# Revit family: Gaius Life Basin_
name_source: partatom
category: Plumbing Fixtures
revit_build: Autodesk Revit Architecture 2012 (Build: 20110916_2132(x64)
units: mm (PartAtom-declared; Revit-internal decimal feet)

## types (20) — shared parameters
Drain Pipe Material = Chrome - Polished
Manufacturer = Korpinen Oy
URL = www.korpinen.com
Vent Connection = No

## per-type parameters (varying)
| type | Basin Type | Cabinet Type | Height | Model |
| 6700 | Gaius Life : 6700 | None | 850 mm  [stored 2.78871 ft] | 6700 Gaius Life |
| 6701 | Gaius Life : 6701 | None | 850 mm  [stored 2.78871 ft] | 6701 Gaius Life |
| 6706 | Gaius Life : 6706 | None | 850 mm  [stored 2.78871 ft] | 6706 Gaius Life |
| 6707 | Gaius Life : 6707 | None | 850 mm  [stored 2.78871 ft] | 6707 Gaius Life |
| 6709 | Gaius Life : 6709 | None | 850 mm  [stored 2.78871 ft] | 6709 Gaius Life |
| 6708 | Gaius Life : 6708 | None | 850 mm  [stored 2.78871 ft] | 6708 Gaius Life |
| 6702 | Gaius Life : 6702 | None | 850 mm  [stored 2.78871 ft] | 6702 Gaius Life |
| 6703 | Gaius Life : 6703 | None | 850 mm  [stored 2.78871 ft] | 6703 Gaius Life |
| 6704 | Gaius Life : 6704 | None | 850 mm  [stored 2.78871 ft] | 6704 Gaius Life |
| 6705 | Gaius Life : 6705 | None | 850 mm  [stored 2.78871 ft] | 6705 Gaius Life |
| 6700 with Drawer Cabinet | Gaius Life : 6700 | Life - Under Basin Cabinet : 2000-1001 | 850 mm  [stored 2.78871 ft] | 6700 Gaius Life + 2000-1001 |
| 6701 with Drawer Cabinet | Gaius Life : 6701 | Life - Under Basin Cabinet : 2000-1001 | 850 mm  [stored 2.78871 ft] | 6701 Gaius Life + 2000-1001 |
| 6702 with Drawer Cabinet | Gaius Life : 6702 | Life - Under Basin Cabinet : 2000-1001 | 850 mm  [stored 2.78871 ft] | 6702 Gaius Life + 2000-1001 |
| 6703 with Drawer Cabinet | Gaius Life : 6703 | Life - Under Basin Cabinet : 2000-1001 | 850 mm  [stored 2.78871 ft] | 6702 Gaius Life + 2000-1001 |
| 6704 with Drawer Cabinet | Gaius Life : 6704 | Life - Under Basin Cabinet : 2000-1001 | 850 mm  [stored 2.78871 ft] | 6704 Gaius Life + 2000-1001 |
| 6705 with Drawer Cabinet | Gaius Life : 6705 | Life - Under Basin Cabinet : 2000-1001 | 850 mm  [stored 2.78871 ft] | 6705 Gaius Life + 2000-1001 |
| 6706 with Drawer Cabinet | Gaius Life : 6706 | Life - Under Basin Cabinet : 2000-1002 | 850 mm  [stored 2.78871 ft] | 6706 Gaius Life + 2000-1002 |
| 6707 with Drawer Cabinet | Gaius Life : 6707 | Life - Under Basin Cabinet : 2000-1002 | 850 mm  [stored 2.78871 ft] | 6707 Gaius Life + 2000-1002 |
| 6708 with Drawer Cabinet | Gaius Life : 6708 | Life - Under Basin Cabinet : 2000-1002 | 850 mm  [stored 2.78871 ft] | 6708 Gaius Life + 2000-1002 |
| 6709 with Drawer Cabinet | Gaius Life : 6709 | Life - Under Basin Cabinet : 2000-1002 | 800 mm  [stored 2.62467 ft] | 6709 Gaius Life + 2000-1002 |

note: [stored X ft] marks values corroborated as IEEE doubles in the binary element streams (Revit-internal decimal feet)

## geometry (parser evidence)
native form markers: Blend x6, Sweep x13
no freeform markers — native parametric forms only
